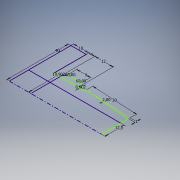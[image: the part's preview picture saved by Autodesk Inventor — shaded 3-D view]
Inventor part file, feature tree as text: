
AUTODESK INVENTOR PART (.ipt)
format: ipt  version: 2016 (Build 200138000, 138)  size: 101,376 bytes
history: native  units: mm
features: sketch x1
ambient origin geometry x8: Origin, YZ Plane, XZ Plane, XY Plane, X Axis, Y Axis, Z Axis, Center Point
feature tree (1):
  sketch  "Sketch2"  dims[d0=10.0mm d1=40.0mm d3=12.5mm d13=4.0mm d16=12.0mm d17=9.0mm d18=60.0deg d19=60.0deg d20=1.0mm d21=0.901924mm d22=19.901924mm d23=30.0mm d25=0.349066mm]
